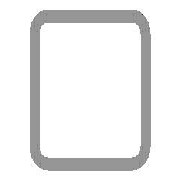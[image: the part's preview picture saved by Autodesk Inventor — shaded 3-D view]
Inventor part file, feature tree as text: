
AUTODESK INVENTOR PART (.ipt)
format: ipt  version: 2025 (Build 290162010, 162A)  size: 133,120 bytes
history: native  units: mm (DEFAULTED — no unit token found)
features: other x4, sketch x1, plane x1
ambient origin geometry x8: Origin, YZ Plane, XZ Plane, XY Plane, X Axis, Y Axis, Z Axis, Center Point
bodies: Solid1 (feature_tree), Body (feature_tree)
feature tree (6):
  parser-record x1  (decoder bookkeeping rows leaked as tree rows — omitted from the tree; the rows remain in map.json)
  other  "Driven Length"
  other  "Start Plane"
  other  "End Plane"
  sketch  "Sketch3"  dims[d3=7000.0mm d4=0.0mm d7=6.0mm d9=80.0mm d11=80.0mm d12=3.0mm d13=-0.0mm d14=7000.0mm d15=40.0mm d16=40.0mm d17=90.0deg d18=7000.0mm]
  plane  "Work Plane3"
